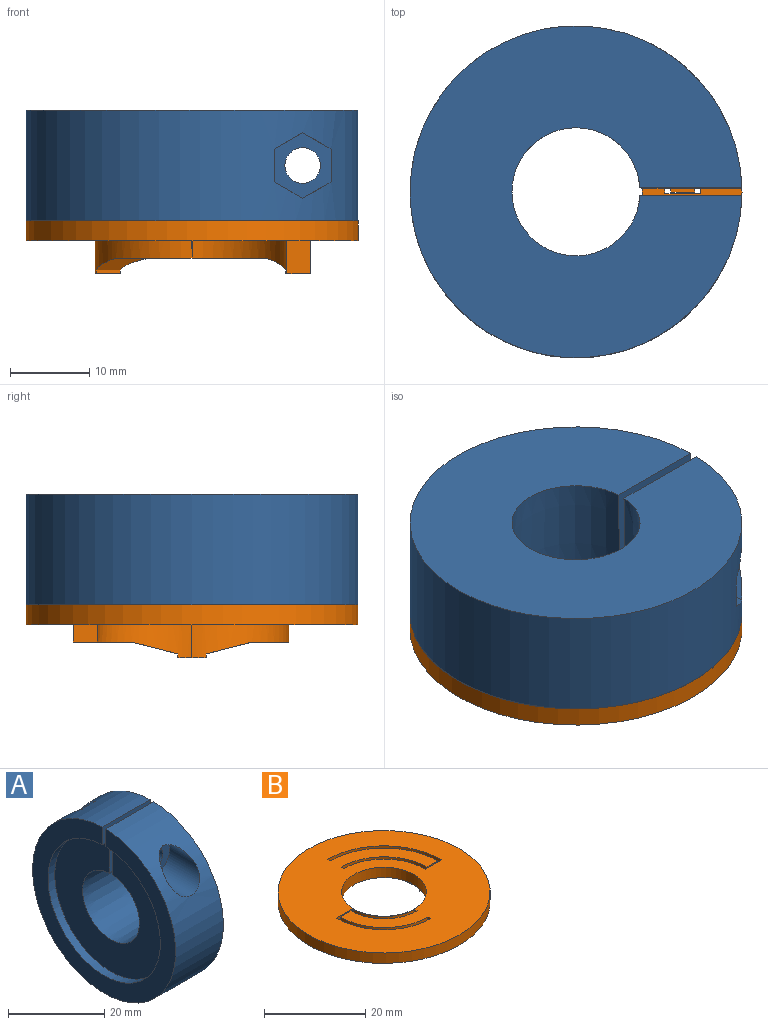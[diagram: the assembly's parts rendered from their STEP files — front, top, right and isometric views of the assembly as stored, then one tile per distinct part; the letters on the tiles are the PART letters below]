
ASSEMBLY  parts=2 mates=1
PART A: 19 faces, bbox 14.1x42.1x42.1 mm
  f0: cylinder r=2.25mm len=7.5mm, axis (0,-1,0), area 106mm2, adj f7,f11
  f1: plane 33x32.99mm, normal (-1,0,0), area 628.1mm2, adj f2,f5,f7,f8
  f2: cone r=8.35mm half-angle=1.2deg, axis (-1,0,0), area 608.3mm2, adj f1,f3,f7,f8
  f3: plane 42x41.99mm, normal (1,0,0), area 1166.4mm2, adj f2,f4,f7,f8
  f4: cylinder r=21mm len=42mm, axis (-1,0,0), area 1692.7mm2, adj f3,f6,f7,f8,f10,f12,f13,f14
  f5: cylinder r=16.5mm len=33mm, axis (-1,0,0), area 205.3mm2, adj f1,f6,f7,f8
  f6: plane 42x41.99mm, normal (-1,0,0), area 525.6mm2, adj f4,f5,f7,f8
  f7: plane 14x12.91mm, normal (0,1,0), area 146.5mm2, adj f0,f1,f2,f3,f4,f5,f6
  f8: plane 14x12.91mm, normal (0,-1,0), area 146.5mm2, adj f1,f2,f3,f4,f5,f6,f9
  f9: cylinder r=2.25mm len=7.5mm, axis (0,-1,0), area 106mm2, adj f8,f18
  f10: cylinder r=4.25mm len=10.6mm, axis (0,-1,0), area 189.4mm2, adj f4,f11
  f11: plane 8.5x8.5mm, normal (0,-1,0), area 40.8mm2, adj f0,f10
  f12: plane 10.24x4.16mm, normal (0,0,1), area 42.6mm2, adj f4,f13,f17,f18
  f13: plane 10.32x3.68mm, normal (-0.87,0,0.5), area 37.6mm2, adj f4,f12,f14,f18
  f14: plane 7.65x3.6mm, normal (-0.87,0,-0.5), area 23.9mm2, adj f4,f13,f15,f18
  f15: plane 4.16x3.46mm, normal (0,0,-1), area 14.4mm2, adj f4,f14,f16,f18
  f16: plane 7.65x3.6mm, normal (0.87,0,-0.5), area 23.9mm2, adj f4,f15,f17,f18
  f17: plane 10.32x3.68mm, normal (0.87,0,0.5), area 37.6mm2, adj f4,f12,f16,f18
  f18: plane 8.31x7.2mm, normal (0,1,0), area 29mm2, adj f9,f12,f13,f14,f15,f16,f17
PART B: 34 faces, bbox 42x42x6.7 mm
  f0: cylinder r=12.25mm len=12.25mm, axis (0,0,-1), area 98.7mm2, adj f2,f3,f16,f17,f27,f31,f32,f33
  f1: cylinder r=9.25mm len=9.25mm, axis (0,0,-1), area 76.8mm2, adj f2,f3,f16,f23,f27,f31,f32,f33
  f2: plane 3x2.2mm, normal (1,0,0), area 6.6mm2, adj f0,f1,f8,f32
  f3: plane 3.18x1.8mm, normal (0,0,-1), area 5.4mm2, adj f0,f1,f16,f33
  f4: cylinder r=12mm len=12mm, axis (0,0,-1), area 96.8mm2, adj f6,f7,f9,f26,f27,f28,f29,f30
  f5: cylinder r=15mm len=15mm, axis (0,0,-1), area 118.9mm2, adj f6,f7,f9,f10,f27,f28,f29,f30
  f6: plane 3x2.2mm, normal (-1,0,0), area 6.6mm2, adj f4,f5,f8,f29
  f7: plane 3.14x1.8mm, normal (0,0,-1), area 5.4mm2, adj f4,f5,f9,f30
  f8: plane 42x42mm, normal (0,0,-1), area 990.1mm2, adj f2,f6,f10,f11,f12,f13,f14,f15
  f9: plane 6.7x3mm, normal (0,-1,0), area 20.1mm2, adj f4,f5,f7,f27
  f10: plane 2.5x0.75mm, normal (1,0,0), area 1.9mm2, adj f5,f8,f11,f27
  f11: cylinder r=15.75mm len=15.75mm, axis (0,0,-1), area 61.9mm2, adj f8,f10,f12,f27
  f12: plane 2.5x0.25mm, normal (-1,0,0), area 0.6mm2, adj f8,f11,f13,f27
  f13: plane 4.5x2.5mm, normal (0,1,0), area 11.3mm2, adj f8,f12,f14,f27
  f14: plane 2.5x0.25mm, normal (1,0,0), area 0.6mm2, adj f8,f13,f15,f27
  f15: cylinder r=11.25mm len=11.25mm, axis (0,0,-1), area 44.2mm2, adj f8,f14,f26,f27
  f16: plane 6.7x3mm, normal (0,1,0), area 20.1mm2, adj f0,f1,f3,f27
  f17: plane 2.5x0.75mm, normal (-1,0,0), area 1.9mm2, adj f0,f8,f18,f27
  f18: cylinder r=13mm len=13mm, axis (0,0,-1), area 51.1mm2, adj f8,f17,f19,f27
  f19: plane 2.5x0.25mm, normal (1,0,0), area 0.6mm2, adj f8,f18,f20,f27
  f20: plane 4.5x2.5mm, normal (0,-1,0), area 11.2mm2, adj f8,f19,f21,f27
  f21: plane 2.5x0.25mm, normal (-1,0,0), area 0.6mm2, adj f8,f20,f22,f27
  f22: cylinder r=8.5mm len=8.5mm, axis (0,0,-1), area 33.4mm2, adj f8,f21,f23,f27
  f23: plane 2.5x0.75mm, normal (-1,0,0), area 1.9mm2, adj f1,f8,f22,f27
  f24: cylinder r=21mm len=42mm, axis (0,0,-1), area 329.9mm2, adj f8,f27
  f25: cylinder r=8.4mm len=16.8mm, axis (0,0,-1), area 131.9mm2, adj f8,f27
  f26: plane 2.5x0.75mm, normal (1,0,0), area 1.9mm2, adj f4,f8,f15,f27
  f27: plane 42x42mm, normal (0,0,1), area 1104.4mm2, adj f0,f1,f4,f5,f9,f10,f11,f12
  f28: plane 5.8x5.61mm, normal (0,0.25,-0.97), area 19.4mm2, adj f4,f5,f29,f30
  f29: plane 12.93x7.4mm, normal (0,0,-1), area 39.4mm2, adj f4,f5,f6,f28
  f30: plane 3.03x0.5mm, normal (0,1,0), area 1.5mm2, adj f4,f5,f7,f28
  f31: plane 6.84x5.8mm, normal (0,-0.25,-0.97), area 20.7mm2, adj f0,f1,f32,f33
  f32: plane 9.61x4.65mm, normal (0,0,-1), area 25.2mm2, adj f0,f1,f2,f31
  f33: plane 3.04x0.5mm, normal (0,-1,0), area 1.5mm2, adj f0,f1,f3,f31
PLACE A rot(axis=(0.71,0,0.71),180deg) t=(-2.5,-4.58,-1.35)mm
PLACE B t=(-2.5,-4.58,-3.85)mm
MATE fastened A.f2 <-> B.f24  axis (0,0,-1) through (-2.5,-4.58,-1.35)mm
